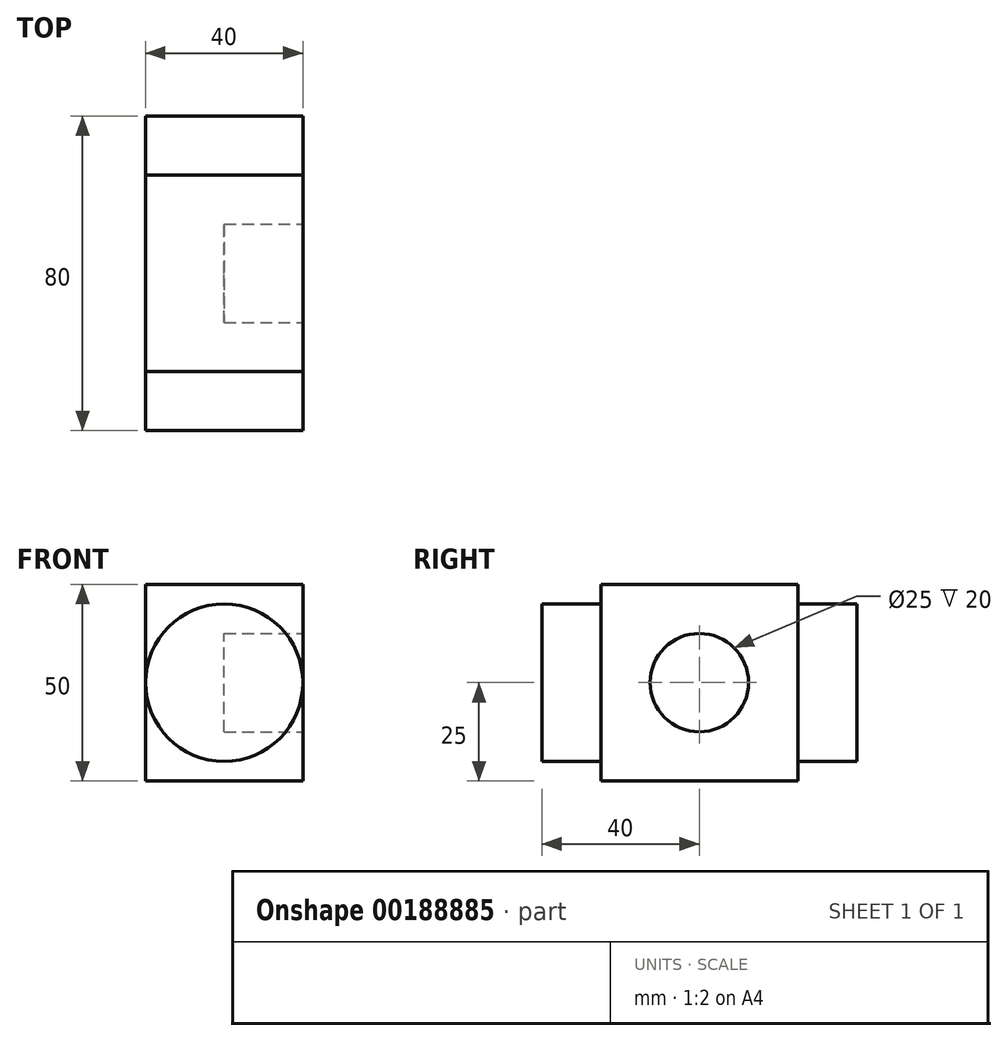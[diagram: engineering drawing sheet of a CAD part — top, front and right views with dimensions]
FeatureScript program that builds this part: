
annotation { "Feature Type Name" : "Feature", "Feature Type Description" : "" }
export const myFeature = defineFeature(function(context is Context, id is Id, definition is map)
    precondition{}
    {
        {
            var Q0;
            Q0=qCreatedBy(makeId("Front.planeOp"),FACE);
            var sketch = newSketch(context, id + "F0", { "sketchPlane" : qUnion([Q0])});
            skCircle(sketch, "E0", {"center": v(0, 0) * mm, "radius": 20 * mm});
            skSolve(sketch);
        }
        {
            var Q0;
            Q0 = qSketchRegion(id + "F0", true);
            extrude(context, id + "F1", {"entities" : qUnion([Q0]), "depth" : 80 * mm});
        }
        {
            var Q0;
            Q0=qCreatedBy(makeId("Front.planeOp"),FACE);
            cPlane(context, id + "F2", {"entities" : qUnion([Q0]), "cplaneType" : CPlaneType.OFFSET, "offset" : 15 * mm, "width" : 150 * mm, "height" : 150 * mm});
        }
        {
            var Q0;
            Q0=qCreatedBy(id+"F2.planeOp",FACE);
            var sketch = newSketch(context, id + "F3", { "sketchPlane" : qUnion([Q0])});
            skLineSegment(sketch, "E1.bottom", {"start": v(-20, -25) * mm, "end": v(20, -25) * mm});
            skLineSegment(sketch, "E1.top", {"start": v(-20, 25) * mm, "end": v(20, 25) * mm});
            skLineSegment(sketch, "E1.left", {"start": v(-20, -25) * mm, "end": v(-20, 25) * mm});
            skLineSegment(sketch, "E1.right", {"start": v(20, -25) * mm, "end": v(20, 25) * mm});
            skPoint(sketch, "E1.middle", {"position": v(0, 0) * mm});
            skSolve(sketch);
        }
        {
            var Q0;
            Q0 = qSketchRegion(id + "F3", true);
            extrude(context, id + "F4", {"entities" : qUnion([Q0]), "operationType" : NewBodyOperationType.ADD, "depth" : 50 * mm});
        }
        {
            var Q0;
            Q0=makeQuery(id+"F4.opExtrude","SWEPT_FACE",FACE,{"disambiguationData":[OSD([sQuery(id+"F3.wireOp",EDGE,"E1.right")])]});
            var sketch = newSketch(context, id + "F5", { "sketchPlane" : qUnion([Q0])});
            skCircle(sketch, "E2", {"center": v(-40, 0) * mm, "radius": 12.5 * mm});
            skSolve(sketch);
        }
        {
            var Q0;
            Q0 = qSketchRegion(id + "F5", true);
            extrude(context, id + "F6", {"entities" : qUnion([Q0]), "operationType" : NewBodyOperationType.REMOVE, "oppositeDirection" : true, "depth" : 20 * mm});
        }
    });
